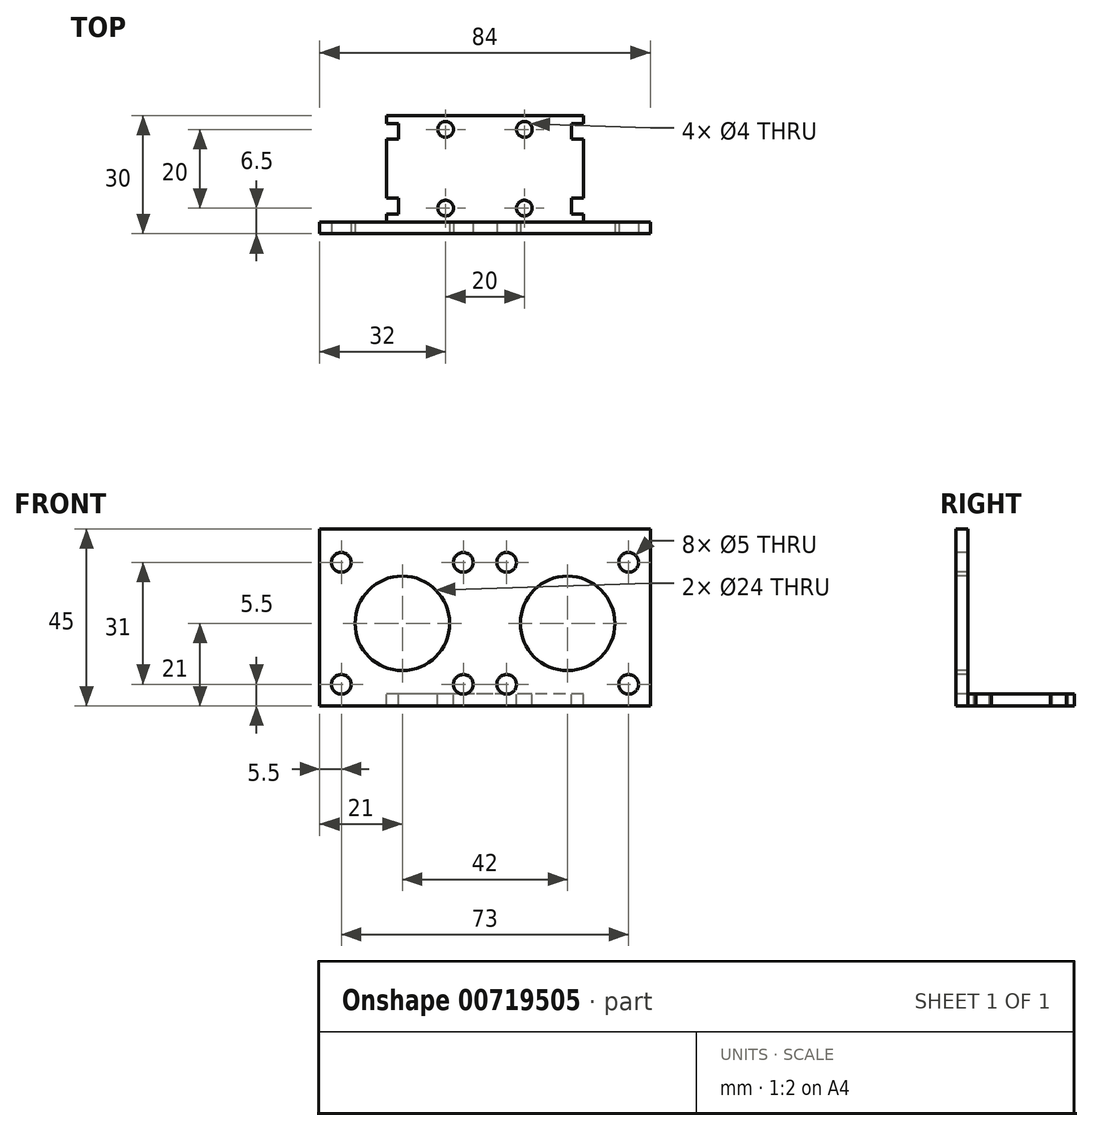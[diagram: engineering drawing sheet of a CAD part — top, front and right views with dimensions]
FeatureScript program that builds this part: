
annotation { "Feature Type Name" : "Feature", "Feature Type Description" : "" }
export const myFeature = defineFeature(function(context is Context, id is Id, definition is map)
    precondition{}
    {
        {
            var Q0;
            Q0=qCreatedBy(makeId("Top.planeOp"),FACE);
            var sketch = newSketch(context, id + "F0", { "sketchPlane" : qUnion([Q0])});
            skLineSegment(sketch, "E0.bottom", {"start": v(21, -15) * mm, "end": v(-21, -15) * mm});
            skLineSegment(sketch, "E0.top", {"start": v(21, 15) * mm, "end": v(-21, 15) * mm});
            skLineSegment(sketch, "E0.left", {"start": v(21, -15) * mm, "end": v(21, 15) * mm});
            skLineSegment(sketch, "E0.right", {"start": v(-21, -15) * mm, "end": v(-21, 15) * mm});
            skPoint(sketch, "E0.middle", {"position": v(0, 0) * mm});
            skLineSegment(sketch, "E1", {"start": v(21, -12) * mm, "end": v(-21, -12) * mm});
            skSolve(sketch);
        }
        {
            var Q0;
            {var subQ0=sQuery(id+"F0.wireOp",EDGE,"E0.top");Q0=makeQuery(id+"F0.imprint","IMPRINT",FACE,{"disambiguationData":[TD([[makeQuery(id+"F0.imprint","IMPRINT",EDGE,{"derivedFrom":subQ0}),1.0]])]});}
            extrude(context, id + "F1", {"entities" : qUnion([Q0]), "depth" : 3 * mm, "offsetDistance" : 25 * mm});
        }
        {
            var Q0;
            {var subQ0=sQuery(id+"F0.wireOp",EDGE,"E0.bottom");Q0=makeQuery(id+"F0.imprint","IMPRINT",FACE,{"disambiguationData":[TD([[makeQuery(id+"F0.imprint","IMPRINT",EDGE,{"derivedFrom":subQ0}),-1.0]])]});}
            extrude(context, id + "F2", {"entities" : qUnion([Q0]), "operationType" : NewBodyOperationType.ADD, "depth" : 45 * mm, "offsetDistance" : 25 * mm});
        }
        {
            var Q0;
            Q0=makeQuery(id+"F1.opExtrude","CAP_FACE",FACE,{"disambiguationData":[OSD([sQuery(id+"F0.wireOp",EDGE,"E0.top"),sQuery(id+"F0.wireOp",EDGE,"E0.left"),sQuery(id+"F0.wireOp",EDGE,"E0.right"),sQuery(id+"F0.wireOp",EDGE,"E1")])],"isStart":false});
            var sketch = newSketch(context, id + "F3", { "sketchPlane" : qUnion([Q0])});
            skLineSegment(sketch, "E2.bottom", {"start": v(10, -8.5) * mm, "end": v(-10, -8.5) * mm});
            skLineSegment(sketch, "E2.top", {"start": v(10, 11.5) * mm, "end": v(-10, 11.5) * mm});
            skLineSegment(sketch, "E2.left", {"start": v(10, -8.5) * mm, "end": v(10, 11.5) * mm});
            skLineSegment(sketch, "E2.right", {"start": v(-10, -8.5) * mm, "end": v(-10, 11.5) * mm});
            skSolve(sketch);
        }
        {
            var Q0;
            Q0=sQuery(id+"F3.wireOp",VERTEX,"E2.bottom.start");
            var Q1;
            Q1=sQuery(id+"F3.wireOp",VERTEX,"E2.left.end");
            var Q2;
            Q2=sQuery(id+"F3.wireOp",VERTEX,"E2.top.end");
            var Q3;
            Q3=sQuery(id+"F3.wireOp",VERTEX,"E2.right.start");
            var Q4;
            Q4=makeQuery(id+"F1.opExtrude","SWEPT_BODY",BODY,{"disambiguationData":[OSD([sQuery(id+"F0.wireOp",EDGE,"E0.top"),sQuery(id+"F0.wireOp",EDGE,"E0.left"),sQuery(id+"F0.wireOp",EDGE,"E0.right"),sQuery(id+"F0.wireOp",EDGE,"E1")])]});
            hole(context, id + "F4", {"style" : HoleStyle.SIMPLE, "endStyle" : HoleEndStyle.THROUGH, "holeDiameter" : 4 * mm, "majorDiameter" : 5 * mm, "isTappedThrough" : true, "tappedDepth" : 12 * mm, "tapClearance" : 3, "locations" : qUnion([Q0, Q1, Q2, Q3]), "scope" : qUnion([Q4])});
        }
        {
            var Q0;
            Q0=makeQuery(id+"F2.opExtrude","SWEPT_FACE",FACE,{"disambiguationData":[OSD([sQuery(id+"F0.wireOp",EDGE,"E1")])]});
            var sketch = newSketch(context, id + "F5", { "sketchPlane" : qUnion([Q0])});
            skLineSegment(sketch, "E3.bottom", {"start": v(15.5, 8.5) * mm, "end": v(-15.5, 8.5) * mm});
            skLineSegment(sketch, "E3.top", {"start": v(15.5, 39.5) * mm, "end": v(-15.5, 39.5) * mm});
            skLineSegment(sketch, "E3.left", {"start": v(15.5, 8.5) * mm, "end": v(15.5, 39.5) * mm});
            skLineSegment(sketch, "E3.right", {"start": v(-15.5, 8.5) * mm, "end": v(-15.5, 39.5) * mm});
            skPoint(sketch, "E3.middle", {"position": v(0, 24) * mm});
            skPoint(sketch, "E3.middle.positionSnap0", {"position": v(-21, 24) * mm});
            skPoint(sketch, "E3.centerSnap0", {"position": v(-21, 24) * mm});
            skSolve(sketch);
        }
        {
            var Q0;
            Q0=sQuery(id+"F5.wireOp",VERTEX,"E3.top.end");
            var Q1;
            Q1=sQuery(id+"F5.wireOp",VERTEX,"E3.bottom.end");
            var Q2;
            Q2=sQuery(id+"F5.wireOp",VERTEX,"E3.left.start");
            var Q3;
            Q3=sQuery(id+"F5.wireOp",VERTEX,"E3.top.start");
            var Q4;
            Q4=makeQuery(id+"F1.opExtrude","SWEPT_BODY",BODY,{"disambiguationData":[OSD([sQuery(id+"F0.wireOp",EDGE,"E0.top"),sQuery(id+"F0.wireOp",EDGE,"E0.left"),sQuery(id+"F0.wireOp",EDGE,"E0.right"),sQuery(id+"F0.wireOp",EDGE,"E1")])]});
            hole(context, id + "F6", {"style" : HoleStyle.SIMPLE, "endStyle" : HoleEndStyle.THROUGH, "holeDiameter" : 5 * mm, "majorDiameter" : 5 * mm, "isTappedThrough" : true, "tappedDepth" : 12 * mm, "tapClearance" : 3, "locations" : qUnion([Q0, Q1, Q2, Q3]), "scope" : qUnion([Q4])});
        }
        {
            var Q0;
            Q0=makeQuery(id+"F2.opExtrude","SWEPT_FACE",FACE,{"disambiguationData":[OSD([sQuery(id+"F0.wireOp",EDGE,"E1")])]});
            var sketch = newSketch(context, id + "F7", { "sketchPlane" : qUnion([Q0])});
            skCircle(sketch, "E4", {"center": v(0, 24) * mm, "radius": 12 * mm});
            skPoint(sketch, "E4.centerSnap0", {"position": v(0, 45) * mm});
            skPoint(sketch, "E4.centerSnap1", {"position": v(-21, 24) * mm});
            skSolve(sketch);
        }
        {
            var Q0;
            Q0=makeQuery(id+"F7.imprint","IMPRINT",FACE,{"disambiguationData":[TD([[makeQuery(id+"F7.imprint","IMPRINT",EDGE,{"derivedFrom":sQuery(id+"F7.wireOp",EDGE,"E4")}),1.0]])]});
            extrude(context, id + "F8", {"entities" : qUnion([Q0]), "operationType" : NewBodyOperationType.REMOVE, "oppositeDirection" : true, "depth" : 25 * mm, "offsetDistance" : 25 * mm});
        }
        {
            var Q0;
            {var subQ0=sQuery(id+"F0.wireOp",EDGE,"E0.right");Q0=makeQuery(id+"F2.boolean.opBoolean","MERGE",FACE,{"derivedFrom":[makeQuery(id+"F1.opExtrude","SWEPT_FACE",FACE,{"disambiguationData":[OSD([subQ0])]}),makeQuery(id+"F2.opExtrude","SWEPT_FACE",FACE,{"disambiguationData":[OSD([subQ0])]})]});}
            var sketch = newSketch(context, id + "F9", { "sketchPlane" : qUnion([Q0])});
            skPoint(sketch, "E5.oppositeSnap0", {"position": v(0, 0) * mm});
            skLineSegment(sketch, "E5.bottom", {"start": v(-15, 3) * mm, "end": v(12, 3) * mm});
            skLineSegment(sketch, "E5.top", {"start": v(-15, 0) * mm, "end": v(12, 0) * mm});
            skLineSegment(sketch, "E5.left", {"start": v(-15, 3) * mm, "end": v(-15, 0) * mm});
            skLineSegment(sketch, "E5.right", {"start": v(12, 3) * mm, "end": v(12, 0) * mm});
            skSolve(sketch);
        }
        {
            var Q0;
            Q0=makeQuery(id+"F9.imprint","IMPRINT",FACE,{"disambiguationData":[TD([[makeQuery(id+"F9.imprint","IMPRINT",EDGE,{"derivedFrom":sQuery(id+"F9.wireOp",EDGE,"E5.bottom")}),1.0]])]});
            extrude(context, id + "F10", {"entities" : qUnion([Q0]), "operationType" : NewBodyOperationType.ADD, "depth" : 4 * mm, "offsetDistance" : 25 * mm});
        }
        {
            var Q0;
            Q0=makeQuery(id+"F10.boolean.opBoolean","MERGE",FACE,{"derivedFrom":[makeQuery(id+"F1.opExtrude","CAP_FACE",FACE,{"disambiguationData":[OSD([sQuery(id+"F0.wireOp",EDGE,"E0.top"),sQuery(id+"F0.wireOp",EDGE,"E0.left"),sQuery(id+"F0.wireOp",EDGE,"E0.right"),sQuery(id+"F0.wireOp",EDGE,"E1")])],"isStart":false}),makeQuery(id+"F10.opExtrude","SWEPT_FACE",FACE,{"disambiguationData":[OSD([sQuery(id+"F9.wireOp",EDGE,"E5.bottom")])]})]});
            var sketch = newSketch(context, id + "F11", { "sketchPlane" : qUnion([Q0])});
            skPoint(sketch, "E6", {"position": v(-22, -6) * mm});
            skPoint(sketch, "E7", {"position": v(-22, 9) * mm});
            skLineSegment(sketch, "E8.bottom", {"start": v(-22, 9) * mm, "end": v(-25, 9) * mm});
            skLineSegment(sketch, "E8.top", {"start": v(-22, 13) * mm, "end": v(-25, 13) * mm});
            skLineSegment(sketch, "E8.left", {"start": v(-22, 9) * mm, "end": v(-22, 13) * mm});
            skLineSegment(sketch, "E8.right", {"start": v(-25, 9) * mm, "end": v(-25, 13) * mm});
            skLineSegment(sketch, "E9.bottom", {"start": v(-22, -6) * mm, "end": v(-25, -6) * mm});
            skLineSegment(sketch, "E9.top", {"start": v(-22, -10) * mm, "end": v(-25, -10) * mm});
            skLineSegment(sketch, "E9.left", {"start": v(-22, -6) * mm, "end": v(-22, -10) * mm});
            skLineSegment(sketch, "E9.right", {"start": v(-25, -6) * mm, "end": v(-25, -10) * mm});
            skSolve(sketch);
        }
        {
            var Q0;
            Q0=makeQuery(id+"F11.imprint","IMPRINT",FACE,{"disambiguationData":[TD([[makeQuery(id+"F11.imprint","IMPRINT",EDGE,{"derivedFrom":sQuery(id+"F11.wireOp",EDGE,"E8.bottom")}),-1.0]])]});
            var Q1;
            Q1=qSketchRegion(id+"F11",true);
            var Q2;
            Q2=makeQuery(id+"F11.imprint","IMPRINT",FACE,{"disambiguationData":[TD([[makeQuery(id+"F11.imprint","IMPRINT",EDGE,{"derivedFrom":sQuery(id+"F11.wireOp",EDGE,"E9.bottom")}),1.0]])]});
            extrude(context, id + "F12", {"entities" : qUnion([Q0, Q1, Q2]), "operationType" : NewBodyOperationType.REMOVE, "oppositeDirection" : true, "depth" : 25 * mm, "offsetDistance" : 25 * mm});
        }
        {
            var Q0;
            {var subQ0=sQuery(id+"F0.wireOp",EDGE,"E0.left");Q0=makeQuery(id+"F2.boolean.opBoolean","MERGE",FACE,{"derivedFrom":[makeQuery(id+"F1.opExtrude","SWEPT_FACE",FACE,{"disambiguationData":[OSD([subQ0])]}),makeQuery(id+"F2.opExtrude","SWEPT_FACE",FACE,{"disambiguationData":[OSD([subQ0])]})]});}
            var sketch = newSketch(context, id + "F13", { "sketchPlane" : qUnion([Q0])});
            skLineSegment(sketch, "E10.bottom", {"start": v(-12, 3) * mm, "end": v(15, 3) * mm});
            skLineSegment(sketch, "E10.top", {"start": v(-12, 0) * mm, "end": v(15, 0) * mm});
            skLineSegment(sketch, "E10.left", {"start": v(-12, 3) * mm, "end": v(-12, 0) * mm});
            skLineSegment(sketch, "E10.right", {"start": v(15, 3) * mm, "end": v(15, 0) * mm});
            skSolve(sketch);
        }
        {
            var Q0;
            Q0=qSketchRegion(id+"F13",true);
            extrude(context, id + "F14", {"entities" : qUnion([Q0]), "operationType" : NewBodyOperationType.ADD, "depth" : 4 * mm, "offsetDistance" : 25 * mm});
        }
        {
            var Q0;
            Q0=makeQuery(id+"F14.boolean.opBoolean","MERGE",FACE,{"derivedFrom":[makeQuery(id+"F10.boolean.opBoolean","MERGE",FACE,{"derivedFrom":[makeQuery(id+"F1.opExtrude","CAP_FACE",FACE,{"disambiguationData":[OSD([sQuery(id+"F0.wireOp",EDGE,"E0.top"),sQuery(id+"F0.wireOp",EDGE,"E0.left"),sQuery(id+"F0.wireOp",EDGE,"E0.right"),sQuery(id+"F0.wireOp",EDGE,"E1")])],"isStart":false}),makeQuery(id+"F10.opExtrude","SWEPT_FACE",FACE,{"disambiguationData":[OSD([sQuery(id+"F9.wireOp",EDGE,"E5.bottom")])]})]}),makeQuery(id+"F14.opExtrude","SWEPT_FACE",FACE,{"disambiguationData":[OSD([sQuery(id+"F13.wireOp",EDGE,"E10.bottom")])]})]});
            var sketch = newSketch(context, id + "F15", { "sketchPlane" : qUnion([Q0])});
            skLineSegment(sketch, "E11.bottom", {"start": v(25, 9) * mm, "end": v(22, 9) * mm});
            skLineSegment(sketch, "E11.top", {"start": v(25, 13) * mm, "end": v(22, 13) * mm});
            skLineSegment(sketch, "E11.left", {"start": v(25, 9) * mm, "end": v(25, 13) * mm});
            skLineSegment(sketch, "E11.right", {"start": v(22, 9) * mm, "end": v(22, 13) * mm});
            skLineSegment(sketch, "E12.bottom", {"start": v(25, -6) * mm, "end": v(22, -6) * mm});
            skLineSegment(sketch, "E12.top", {"start": v(25, -10) * mm, "end": v(22, -10) * mm});
            skLineSegment(sketch, "E12.left", {"start": v(25, -6) * mm, "end": v(25, -10) * mm});
            skLineSegment(sketch, "E12.right", {"start": v(22, -6) * mm, "end": v(22, -10) * mm});
            skSolve(sketch);
        }
        {
            var Q0;
            Q0=makeQuery(id+"F15.imprint","IMPRINT",FACE,{"disambiguationData":[TD([[makeQuery(id+"F15.imprint","IMPRINT",EDGE,{"derivedFrom":sQuery(id+"F15.wireOp",EDGE,"E11.bottom")}),-1.0]])]});
            var Q1;
            Q1=makeQuery(id+"F15.imprint","IMPRINT",FACE,{"disambiguationData":[TD([[makeQuery(id+"F15.imprint","IMPRINT",EDGE,{"derivedFrom":sQuery(id+"F15.wireOp",EDGE,"E12.bottom")}),1.0]])]});
            extrude(context, id + "F16", {"entities" : qUnion([Q0, Q1]), "operationType" : NewBodyOperationType.REMOVE, "oppositeDirection" : true, "depth" : 25 * mm, "offsetDistance" : 25 * mm});
        }
        {
            var Q0;
            {var subQ0=sQuery(id+"F0.wireOp",EDGE,"E0.left");Q0=makeQuery(id+"F2.boolean.opBoolean","MERGE",FACE,{"derivedFrom":[makeQuery(id+"F1.opExtrude","SWEPT_FACE",FACE,{"disambiguationData":[OSD([subQ0])]}),makeQuery(id+"F2.opExtrude","SWEPT_FACE",FACE,{"disambiguationData":[OSD([subQ0])]})]});}
            var Q1;
            {var subQ0=sQuery(id+"F0.wireOp",EDGE,"E0.right");Q1=makeQuery(id+"F2.boolean.opBoolean","MERGE",FACE,{"derivedFrom":[makeQuery(id+"F1.opExtrude","SWEPT_FACE",FACE,{"disambiguationData":[OSD([subQ0])]}),makeQuery(id+"F2.opExtrude","SWEPT_FACE",FACE,{"disambiguationData":[OSD([subQ0])]})]});}
            extrude(context, id + "F17", {"entities" : qUnion([Q0, Q1]), "operationType" : NewBodyOperationType.ADD, "depth" : 21 * mm, "offsetDistance" : 25 * mm, "hasSecondDirection" : true, "secondDirectionOppositeDirection" : true, "secondDirectionDepth" : 21 * mm});
        }
        {
            var Q0;
            {var subQ0=sQuery(id+"F0.wireOp",EDGE,"E0.bottom");Q0=makeQuery(id+"F17.boolean.opBoolean","MERGE",FACE,{"derivedFrom":[makeQuery(id+"F2.opExtrude","SWEPT_FACE",FACE,{"disambiguationData":[OSD([subQ0])]}),makeQuery(id+"F17.opExtrude","SWEPT_FACE",FACE,{"disambiguationData":[OSD([subQ0,sQuery(id+"F0.wireOp",EDGE,"E0.left")])]}),makeQuery(id+"F17.opExtrude","SWEPT_FACE",FACE,{"disambiguationData":[OSD([subQ0,sQuery(id+"F0.wireOp",EDGE,"E0.right")])]})]});}
            var sketch = newSketch(context, id + "F18", { "sketchPlane" : qUnion([Q0])});
            skPoint(sketch, "E13", {"position": v(21, 21) * mm});
            skPoint(sketch, "E14", {"position": v(-21, 21) * mm});
            skLineSegment(sketch, "E15.bottom", {"start": v(5.5, 36.5) * mm, "end": v(36.5, 36.5) * mm});
            skLineSegment(sketch, "E15.top", {"start": v(5.5, 5.5) * mm, "end": v(36.5, 5.5) * mm});
            skLineSegment(sketch, "E15.left", {"start": v(5.5, 36.5) * mm, "end": v(5.5, 5.5) * mm});
            skLineSegment(sketch, "E15.right", {"start": v(36.5, 36.5) * mm, "end": v(36.5, 5.5) * mm});
            skLineSegment(sketch, "E16.bottom", {"start": v(-5.5, 5.5) * mm, "end": v(-36.5, 5.5) * mm});
            skLineSegment(sketch, "E16.top", {"start": v(-5.5, 36.5) * mm, "end": v(-36.5, 36.5) * mm});
            skLineSegment(sketch, "E16.left", {"start": v(-5.5, 5.5) * mm, "end": v(-5.5, 36.5) * mm});
            skLineSegment(sketch, "E16.right", {"start": v(-36.5, 5.5) * mm, "end": v(-36.5, 36.5) * mm});
            skCircle(sketch, "E17", {"center": v(-21, 21) * mm, "radius": 12 * mm});
            skCircle(sketch, "E18", {"center": v(21, 21) * mm, "radius": 12 * mm});
            skSolve(sketch);
        }
        {
            var Q0;
            Q0=makeQuery(id+"F18.imprint","IMPRINT",FACE,{"disambiguationData":[TD([[makeQuery(id+"F18.imprint","IMPRINT",EDGE,{"derivedFrom":sQuery(id+"F18.wireOp",EDGE,"E18")}),1.0]])]});
            var Q1;
            Q1=makeQuery(id+"F18.imprint","IMPRINT",FACE,{"disambiguationData":[TD([[makeQuery(id+"F18.imprint","IMPRINT",EDGE,{"derivedFrom":sQuery(id+"F18.wireOp",EDGE,"E17")}),1.0]])]});
            extrude(context, id + "F19", {"entities" : qUnion([Q0, Q1]), "operationType" : NewBodyOperationType.REMOVE, "oppositeDirection" : true, "depth" : 25 * mm, "offsetDistance" : 25 * mm});
        }
        {
            var Q0;
            Q0=sQuery(id+"F18.wireOp",VERTEX,"E15.right.end");
            var Q1;
            Q1=sQuery(id+"F18.wireOp",VERTEX,"E15.left.end");
            var Q2;
            Q2=sQuery(id+"F18.wireOp",VERTEX,"E15.bottom.end");
            var Q3;
            Q3=sQuery(id+"F18.wireOp",VERTEX,"E16.right.start");
            var Q4;
            Q4=sQuery(id+"F18.wireOp",VERTEX,"E16.bottom.start");
            var Q5;
            Q5=sQuery(id+"F18.wireOp",VERTEX,"E16.left.end");
            var Q6;
            Q6=sQuery(id+"F18.wireOp",VERTEX,"E16.right.end");
            var Q7;
            Q7=sQuery(id+"F18.wireOp",VERTEX,"E15.left.start");
            var Q8;
            Q8=makeQuery(id+"F1.opExtrude","SWEPT_BODY",BODY,{"disambiguationData":[OSD([sQuery(id+"F0.wireOp",EDGE,"E0.top"),sQuery(id+"F0.wireOp",EDGE,"E0.left"),sQuery(id+"F0.wireOp",EDGE,"E0.right"),sQuery(id+"F0.wireOp",EDGE,"E1")])]});
            hole(context, id + "F20", {"style" : HoleStyle.SIMPLE, "endStyle" : HoleEndStyle.THROUGH, "holeDiameter" : 5 * mm, "majorDiameter" : 5 * mm, "isTappedThrough" : true, "tappedDepth" : 12 * mm, "tapClearance" : 3, "locations" : qUnion([Q0, Q1, Q2, Q3, Q4, Q5, Q6, Q7]), "scope" : qUnion([Q8])});
        }
    });
